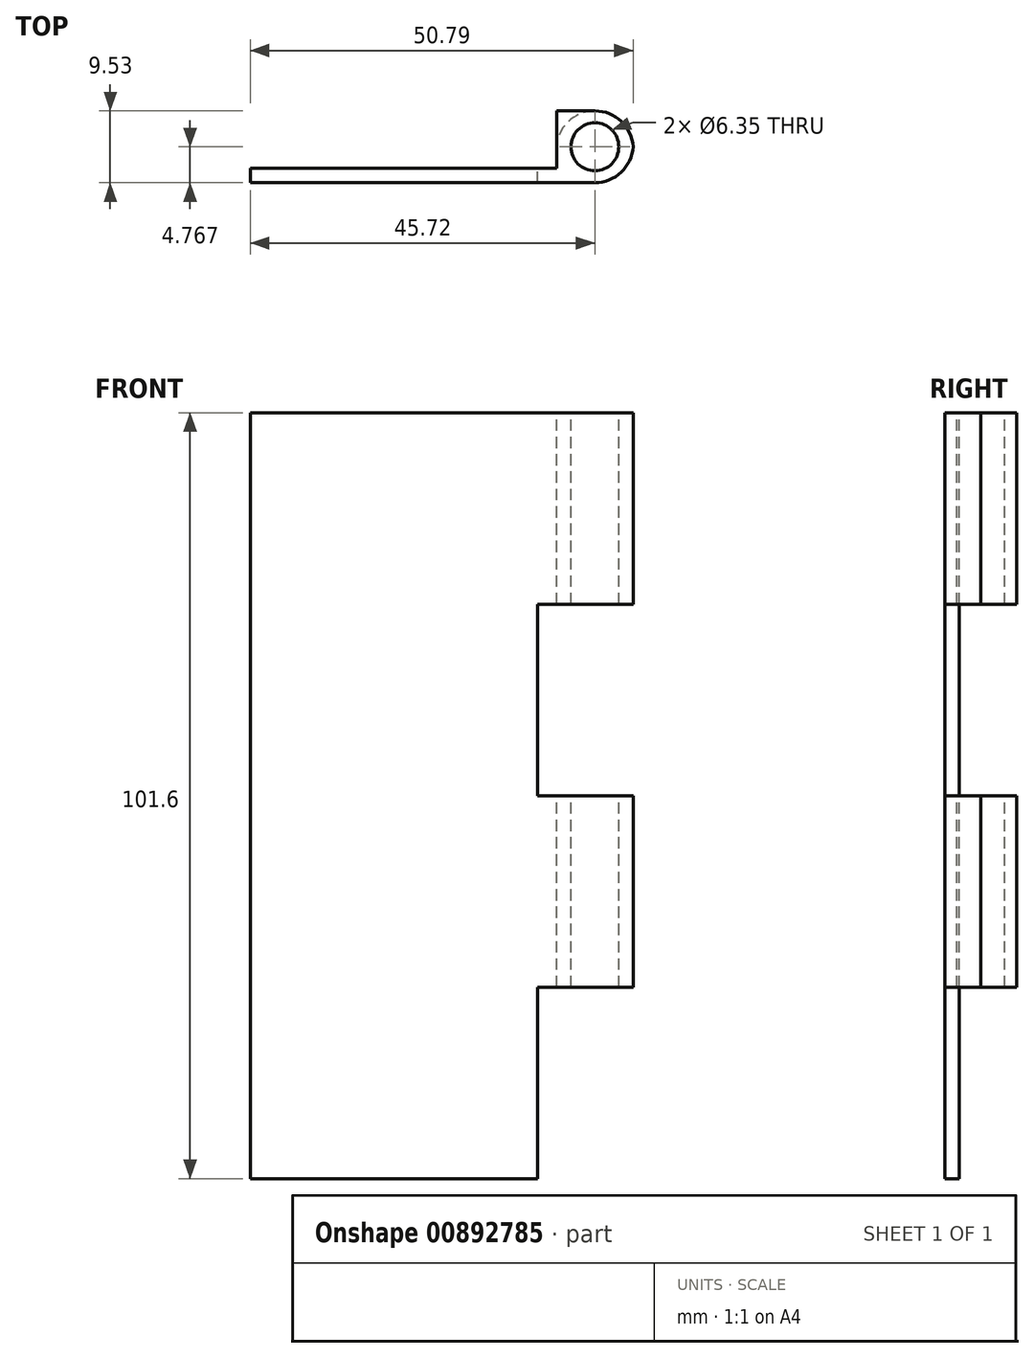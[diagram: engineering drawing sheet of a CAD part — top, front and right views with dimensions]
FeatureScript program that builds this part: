
annotation { "Feature Type Name" : "Feature", "Feature Type Description" : "" }
export const myFeature = defineFeature(function(context is Context, id is Id, definition is map)
    precondition{}
    {
        {
            var Q0;
            Q0=qCreatedBy(makeId("Front.planeOp"),FACE);
            var sketch = newSketch(context, id + "F0", { "sketchPlane" : qUnion([Q0])});
            skLineSegment(sketch, "E0.bottom", {"start": v(25.4, 50.8) * mm, "end": v(-25.4, 50.8) * mm});
            skLineSegment(sketch, "E0.top", {"start": v(25.4, -50.8) * mm, "end": v(-25.4, -50.8) * mm});
            skLineSegment(sketch, "E0.left", {"start": v(25.4, 50.8) * mm, "end": v(25.4, -50.8) * mm});
            skLineSegment(sketch, "E0.right", {"start": v(-25.4, 50.8) * mm, "end": v(-25.4, -50.8) * mm});
            skPoint(sketch, "E0.middle", {"position": v(0, 0) * mm});
            skLineSegment(sketch, "E1.bottom", {"start": v(12.7, 50.8) * mm, "end": v(25.4, 50.8) * mm});
            skLineSegment(sketch, "E1.top", {"start": v(12.7, 25.4) * mm, "end": v(25.4, 25.4) * mm});
            skLineSegment(sketch, "E1.left", {"start": v(12.7, 50.8) * mm, "end": v(12.7, 25.4) * mm});
            skLineSegment(sketch, "E1.right", {"start": v(25.4, 50.8) * mm, "end": v(25.4, 25.4) * mm});
            skLineSegment(sketch, "E2.top", {"start": v(12.7, 0) * mm, "end": v(25.4, 0) * mm});
            skLineSegment(sketch, "E2.left", {"start": v(12.7, 25.4) * mm, "end": v(12.7, 0) * mm});
            skLineSegment(sketch, "E2.right", {"start": v(25.4, 25.4) * mm, "end": v(25.4, 0) * mm});
            skLineSegment(sketch, "E3.top", {"start": v(12.7, -25.4) * mm, "end": v(25.4, -25.4) * mm});
            skLineSegment(sketch, "E3.left", {"start": v(12.7, 0) * mm, "end": v(12.7, -25.4) * mm});
            skLineSegment(sketch, "E3.right", {"start": v(25.4, 0) * mm, "end": v(25.4, -25.4) * mm});
            skLineSegment(sketch, "E4.top", {"start": v(12.7, -50.8) * mm, "end": v(25.4, -50.8) * mm});
            skLineSegment(sketch, "E4.left", {"start": v(12.7, -25.4) * mm, "end": v(12.7, -50.8) * mm});
            skLineSegment(sketch, "E4.right", {"start": v(25.4, -25.4) * mm, "end": v(25.4, -50.8) * mm});
            skSolve(sketch);
        }
        {
            var Q0;
            {var subQ4=sQuery(id+"F0.wireOp",EDGE,"E1.top");Q0=makeQuery(id+"F0.imprint","IMPRINT",FACE,{"disambiguationData":[TD([[makeQuery(id+"F0.imprint","IMPRINT",EDGE,{"derivedFrom":subQ4}),1.0]])]});}
            var Q1;
            {var subQ0=sQuery(id+"F0.wireOp",EDGE,"E0.right");Q1=makeQuery(id+"F0.imprint","IMPRINT",FACE,{"disambiguationData":[TD([[makeQuery(id+"F0.imprint","IMPRINT",EDGE,{"derivedFrom":subQ0}),1.0]])]});}
            var Q2;
            {var subQ2=sQuery(id+"F0.wireOp",EDGE,"E2.top");Q2=makeQuery(id+"F0.imprint","IMPRINT",FACE,{"disambiguationData":[TD([[makeQuery(id+"F0.imprint","IMPRINT",EDGE,{"derivedFrom":subQ2}),-1.0]])]});}
            extrude(context, id + "F1", {"entities" : qUnion([Q0, Q1, Q2]), "depth" : 9.52 * mm, "offsetDistance" : 25.4 * mm});
        }
        {
            var Q0;
            {var subQ0=sQuery(id+"F0.wireOp",EDGE,"E0.left");Q0=makeQuery(id+"F1.opExtrude","CAP_EDGE",EDGE,{"disambiguationData":[OSD([subQ0]),TDD([makeQuery(id+"F0.imprint","IMPRINT",EDGE,{"disambiguationData":[TD([[makeQuery(id+"F0.imprint","INTERSECT",VERTEX,{"derivedFrom":[subQ0,sQuery(id+"F0.wireOp",EDGE,"E1.top")]}),1.0]])],"derivedFrom":subQ0})])],"isStart":true});}
            var Q1;
            {var subQ0=sQuery(id+"F0.wireOp",EDGE,"E0.left");Q1=makeQuery(id+"F1.opExtrude","CAP_EDGE",EDGE,{"disambiguationData":[OSD([subQ0]),TDD([makeQuery(id+"F0.imprint","IMPRINT",EDGE,{"disambiguationData":[TD([[makeQuery(id+"F0.imprint","INTERSECT",VERTEX,{"derivedFrom":[subQ0,sQuery(id+"F0.wireOp",EDGE,"E3.top")]}),1.0]])],"derivedFrom":subQ0})])],"isStart":true});}
            var Q2;
            {var subQ0=sQuery(id+"F0.wireOp",EDGE,"E0.left");Q2=makeQuery(id+"F1.opExtrude","CAP_EDGE",EDGE,{"disambiguationData":[OSD([subQ0]),TDD([makeQuery(id+"F0.imprint","IMPRINT",EDGE,{"disambiguationData":[TD([[makeQuery(id+"F0.imprint","INTERSECT",VERTEX,{"derivedFrom":[subQ0,sQuery(id+"F0.wireOp",EDGE,"E3.top")]}),1.0]])],"derivedFrom":subQ0})])],"isStart":false});}
            var Q3;
            {var subQ0=sQuery(id+"F0.wireOp",EDGE,"E0.left");Q3=makeQuery(id+"F1.opExtrude","CAP_EDGE",EDGE,{"disambiguationData":[OSD([subQ0]),TDD([makeQuery(id+"F0.imprint","IMPRINT",EDGE,{"disambiguationData":[TD([[makeQuery(id+"F0.imprint","INTERSECT",VERTEX,{"derivedFrom":[subQ0,sQuery(id+"F0.wireOp",EDGE,"E1.top")]}),1.0]])],"derivedFrom":subQ0})])],"isStart":false});}
            fillet(context, id + "F2", {"entities" : qUnion([Q0, Q1, Q2, Q3]), "radius" : 5.08 * mm, "tangentPropagation" : true, "allowEdgeOverflow" : false});
        }
        {
            var Q0;
            Q0=makeQuery(id+"F1.opExtrude","SWEPT_FACE",FACE,{"disambiguationData":[OSD([sQuery(id+"F0.wireOp",EDGE,"E0.bottom")])]});
            var sketch = newSketch(context, id + "F3", { "sketchPlane" : qUnion([Q0])});
            skPoint(sketch, "E5", {"position": v(-25.4, -4.76) * mm});
            skLineSegment(sketch, "E6", {"start": v(-25.4, -4.76) * mm, "end": v(25.4, -4.76) * mm, "construction": true});
            skCircle(sketch, "E7", {"center": v(20.32, -4.76) * mm, "radius": 3.18 * mm});
            skSolve(sketch);
        }
        {
            var Q0;
            Q0=makeQuery(id+"F3.imprint","IMPRINT",FACE,{"disambiguationData":[TD([[makeQuery(id+"F3.imprint","IMPRINT",EDGE,{"derivedFrom":sQuery(id+"F3.wireOp",EDGE,"E7")}),1.0]])]});
            var Q1;
            Q1 = qSketchRegion(id + "F3", true);
            extrude(context, id + "F4", {"entities" : qUnion([Q0, Q1]), "operationType" : NewBodyOperationType.REMOVE, "endBound" : BoundingType.THROUGH_ALL, "oppositeDirection" : true, "depth" : 25.4 * mm, "offsetDistance" : 25.4 * mm});
        }
        {
            var Q0;
            Q0=makeQuery(id+"F1.opExtrude","SWEPT_FACE",FACE,{"disambiguationData":[OSD([sQuery(id+"F0.wireOp",EDGE,"E0.bottom")])]});
            var sketch = newSketch(context, id + "F5", { "sketchPlane" : qUnion([Q0])});
            skLineSegment(sketch, "E8.bottom", {"start": v(15.24, 0) * mm, "end": v(-25.4, 0) * mm});
            skLineSegment(sketch, "E8.top", {"start": v(15.24, -7.62) * mm, "end": v(-25.4, -7.62) * mm});
            skLineSegment(sketch, "E8.left", {"start": v(15.24, 0) * mm, "end": v(15.24, -7.62) * mm});
            skLineSegment(sketch, "E8.right", {"start": v(-25.4, 0) * mm, "end": v(-25.4, -7.62) * mm});
            skSolve(sketch);
        }
        {
            var Q0;
            Q0 = qSketchRegion(id + "F5", true);
            extrude(context, id + "F6", {"entities" : qUnion([Q0]), "operationType" : NewBodyOperationType.REMOVE, "endBound" : BoundingType.THROUGH_ALL, "oppositeDirection" : true, "depth" : 25.4 * mm, "offsetDistance" : 25.4 * mm});
        }
        {
            var Q0;
            {var subQ0=sQuery(id+"F0.wireOp",EDGE,"E0.bottom");var subQ2=sQuery(id+"F5.wireOp",EDGE,"E8.left");Q0=makeQuery(id+"F6.boolean.opBoolean","COPY",EDGE,{"disambiguationData":[TD([makeQuery(id+"F1.opExtrude","SWEPT_FACE",FACE,{"disambiguationData":[OSD([subQ0])]})])],"derivedFrom":makeQuery(id+"F6.opExtrude","SWEPT_EDGE",EDGE,{"disambiguationData":[OSD([subQ0,sQuery(id+"F5.wireOp",EDGE,"E8.bottom"),subQ2])]})});}
            var Q1;
            {var subQ1=sQuery(id+"F0.wireOp",EDGE,"E2.top");var subQ2=sQuery(id+"F0.wireOp",EDGE,"E0.bottom");var subQ3=sQuery(id+"F5.wireOp",EDGE,"E8.left");Q1=makeQuery(id+"F6.boolean.opBoolean","COPY",EDGE,{"disambiguationData":[TD([makeQuery(id+"F1.opExtrude","SWEPT_FACE",FACE,{"disambiguationData":[OSD([subQ1])]})])],"derivedFrom":makeQuery(id+"F6.opExtrude","SWEPT_EDGE",EDGE,{"disambiguationData":[OSD([subQ2,sQuery(id+"F5.wireOp",EDGE,"E8.bottom"),subQ3])]})});}
            fillet(context, id + "F7", {"entities" : qUnion([Q0, Q1]), "radius" : 5.08 * mm, "tangentPropagation" : true, "allowEdgeOverflow" : false});
        }
    });
